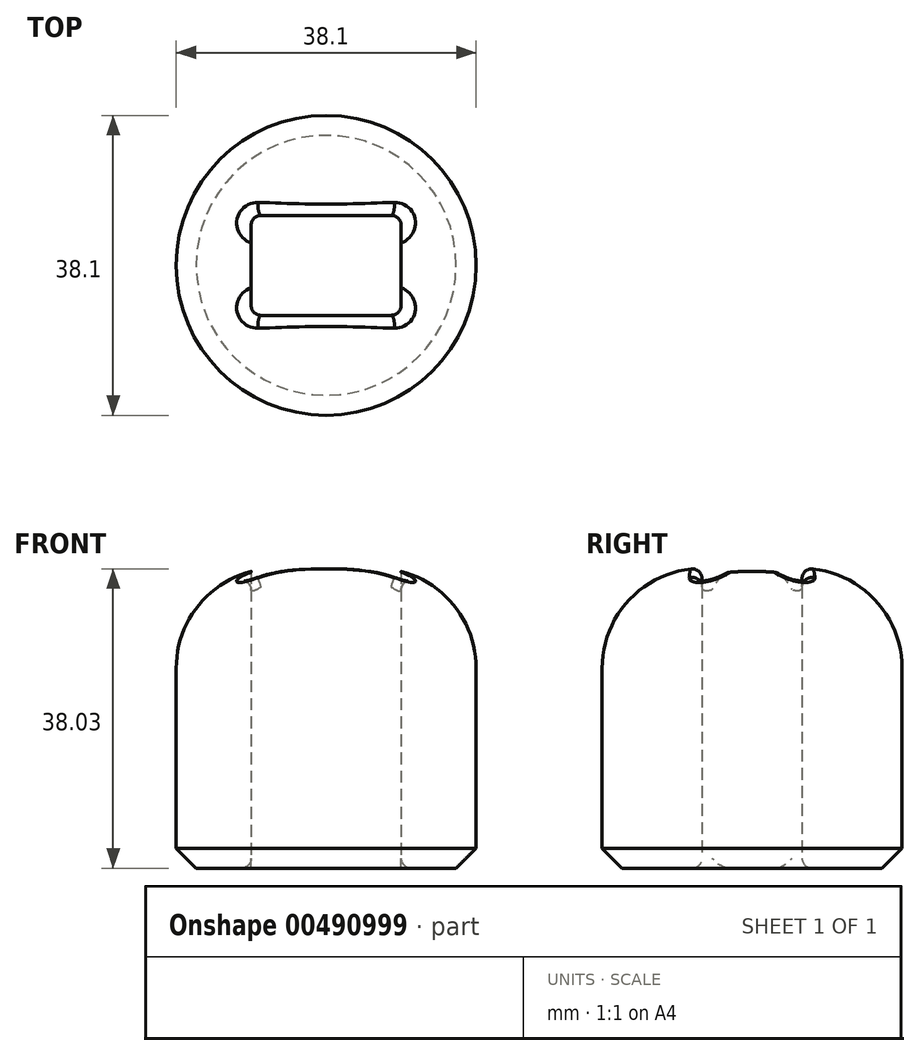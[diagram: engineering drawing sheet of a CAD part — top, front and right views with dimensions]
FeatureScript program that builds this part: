
annotation { "Feature Type Name" : "Feature", "Feature Type Description" : "" }
export const myFeature = defineFeature(function(context is Context, id is Id, definition is map)
    precondition{}
    {
        {
            var Q0;
            Q0=qCreatedBy(makeId("Top.planeOp"),FACE);
            var sketch = newSketch(context, id + "F0", { "sketchPlane" : qUnion([Q0])});
            skCircle(sketch, "E0", {"center": v(0, 0) * mm, "radius": 19.05 * mm});
            skSolve(sketch);
        }
        {
            var Q0;
            Q0=makeQuery(id+"F0.imprint","IMPRINT",FACE,{"disambiguationData":[TD([[makeQuery(id+"F0.imprint","IMPRINT",EDGE,{"derivedFrom":sQuery(id+"F0.wireOp",EDGE,"E0")}),1.0]])]});
            extrude(context, id + "F1", {"entities" : qUnion([Q0]), "depth" : 38.1 * mm});
        }
        {
            var Q0;
            Q0=makeQuery(id+"F1.opExtrude","CAP_EDGE",EDGE,{"disambiguationData":[OSD([sQuery(id+"F0.wireOp",EDGE,"E0")])],"isStart":false});
            fillet(context, id + "F2", {"entities" : qUnion([Q0]), "radius" : 12.7 * mm, "tangentPropagation" : true, "allowEdgeOverflow" : false});
        }
        {
            var Q0;
            Q0=makeQuery(id+"F1.opExtrude","CAP_EDGE",EDGE,{"disambiguationData":[OSD([sQuery(id+"F0.wireOp",EDGE,"E0")])],"isStart":true});
            chamfer(context, id + "F3", {"entities" : qUnion([Q0]), "width" : 2.54 * mm, "tangentPropagation" : true});
        }
        {
            var Q0;
            Q0=makeQuery(id+"F1.opExtrude","CAP_FACE",FACE,{"disambiguationData":[OSD([sQuery(id+"F0.wireOp",EDGE,"E0")])],"isStart":true});
            var sketch = newSketch(context, id + "F4", { "sketchPlane" : qUnion([Q0])});
            skLineSegment(sketch, "E1.bottom", {"start": v(9.53, 6.35) * mm, "end": v(-9.53, 6.35) * mm});
            skLineSegment(sketch, "E1.top", {"start": v(9.53, -6.35) * mm, "end": v(-9.53, -6.35) * mm});
            skLineSegment(sketch, "E1.left", {"start": v(9.53, 6.35) * mm, "end": v(9.53, -6.35) * mm});
            skLineSegment(sketch, "E1.right", {"start": v(-9.53, 6.35) * mm, "end": v(-9.53, -6.35) * mm});
            skPoint(sketch, "E1.middle", {"position": v(0, 0) * mm});
            skSolve(sketch);
        }
        {
            var Q0;
            Q0 = qSketchRegion(id + "F4", true);
            extrude(context, id + "F5", {"entities" : qUnion([Q0]), "operationType" : NewBodyOperationType.REMOVE, "oppositeDirection" : true, "depth" : 57.15 * mm});
        }
        {
            var Q0;
            Q0=makeQuery(id+"F5.boolean.opBoolean","COPY",FACE,{"derivedFrom":makeQuery(id+"F5.opExtrude","SWEPT_FACE",FACE,{"disambiguationData":[OSD([sQuery(id+"F4.wireOp",EDGE,"E1.bottom")])]})});
            var Q1;
            Q1=makeQuery(id+"F5.boolean.opBoolean","COPY",FACE,{"derivedFrom":makeQuery(id+"F5.opExtrude","SWEPT_FACE",FACE,{"disambiguationData":[OSD([sQuery(id+"F4.wireOp",EDGE,"E1.top")])]})});
            fillet(context, id + "F6", {"entities" : qUnion([Q0, Q1]), "radius" : 1.27 * mm, "tangentPropagation" : true, "allowEdgeOverflow" : false});
        }
    });
